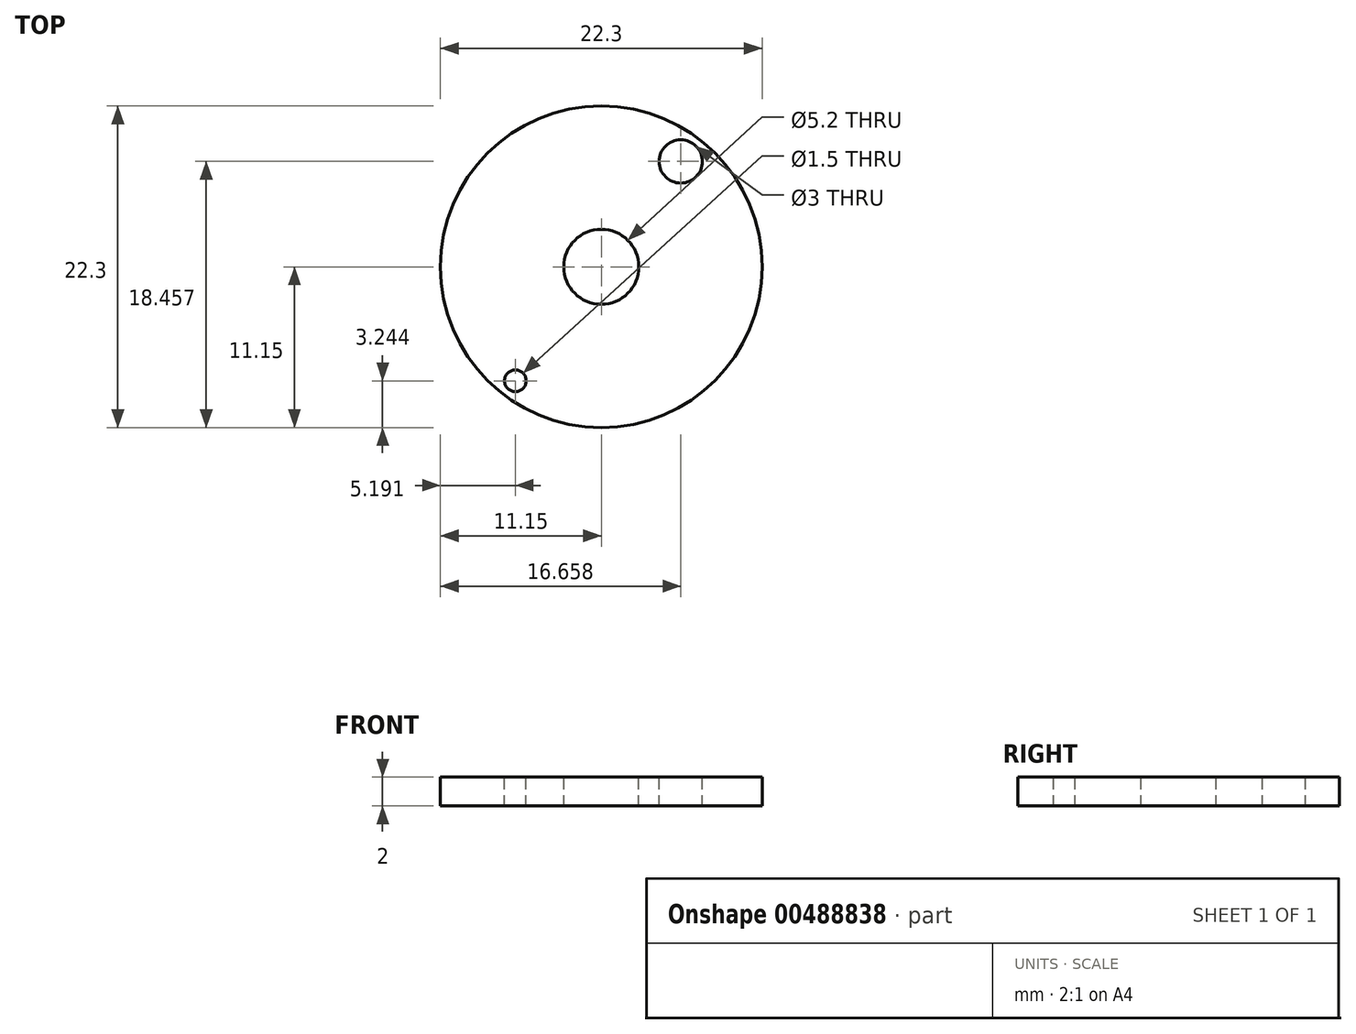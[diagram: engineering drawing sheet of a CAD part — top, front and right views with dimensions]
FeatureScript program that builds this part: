
annotation { "Feature Type Name" : "Feature", "Feature Type Description" : "" }
export const myFeature = defineFeature(function(context is Context, id is Id, definition is map)
    precondition{}
    {
        {
            var Q0;
            Q0=qCreatedBy(makeId("Top.planeOp"),FACE);
            var sketch = newSketch(context, id + "F0", { "sketchPlane" : qUnion([Q0])});
            skCircle(sketch, "E0", {"center": v(0, 0) * mm, "radius": 11.15 * mm});
            skSolve(sketch);
        }
        {
            var Q0;
            Q0=makeQuery(id+"F0.imprint","IMPRINT",FACE,{"disambiguationData":[TD([[makeQuery(id+"F0.imprint","IMPRINT",EDGE,{"derivedFrom":sQuery(id+"F0.wireOp",EDGE,"E0")}),1.0]])]});
            extrude(context, id + "F1", {"entities" : qUnion([Q0]), "offsetDistance" : 25 * mm, "depth" : 2 * mm});
        }
        {
            var Q0;
            Q0=makeQuery(id+"F1.opExtrude","CAP_FACE",FACE,{"disambiguationData":[OSD([sQuery(id+"F0.wireOp",EDGE,"E0")])],"isStart":false});
            var sketch = newSketch(context, id + "F2", { "sketchPlane" : qUnion([Q0])});
            skCircle(sketch, "E1", {"center": v(5.5, 7.3) * mm, "radius": 1.5 * mm});
            skCircle(sketch, "E2.1.0", {"center": v(-5.96, -7.9) * mm, "radius": 0.75 * mm});
            skPoint(sketch, "E2.center", {"position": v(0, 0) * mm});
            skCircle(sketch, "E3", {"center": v(0, 0) * mm, "radius": 2.6 * mm});
            skLineSegment(sketch, "E4", {"start": v(-5.96, -7.9) * mm, "end": v(0, 0) * mm, "construction": true});
            skSolve(sketch);
        }
        {
            var Q0;
            Q0=makeQuery(id+"F2.imprint","IMPRINT",FACE,{"disambiguationData":[TD([[makeQuery(id+"F2.imprint","IMPRINT",EDGE,{"derivedFrom":sQuery(id+"F2.wireOp",EDGE,"E2.7.0")}),1.0]])]});
            var Q1;
            Q1=makeQuery(id+"F2.imprint","IMPRINT",FACE,{"disambiguationData":[TD([[makeQuery(id+"F2.imprint","IMPRINT",EDGE,{"derivedFrom":sQuery(id+"F2.wireOp",EDGE,"E1")}),1.0]])]});
            var Q2;
            Q2=makeQuery(id+"F2.imprint","IMPRINT",FACE,{"disambiguationData":[TD([[makeQuery(id+"F2.imprint","IMPRINT",EDGE,{"derivedFrom":sQuery(id+"F2.wireOp",EDGE,"E2.1.0")}),1.0]])]});
            var Q3;
            Q3=makeQuery(id+"F2.imprint","IMPRINT",FACE,{"disambiguationData":[TD([[makeQuery(id+"F2.imprint","IMPRINT",EDGE,{"derivedFrom":sQuery(id+"F2.wireOp",EDGE,"E2.2.0")}),1.0]])]});
            var Q4;
            Q4=makeQuery(id+"F2.imprint","IMPRINT",FACE,{"disambiguationData":[TD([[makeQuery(id+"F2.imprint","IMPRINT",EDGE,{"derivedFrom":sQuery(id+"F2.wireOp",EDGE,"E2.3.0")}),1.0]])]});
            var Q5;
            Q5=makeQuery(id+"F2.imprint","IMPRINT",FACE,{"disambiguationData":[TD([[makeQuery(id+"F2.imprint","IMPRINT",EDGE,{"derivedFrom":sQuery(id+"F2.wireOp",EDGE,"E2.4.0")}),1.0]])]});
            var Q6;
            Q6=makeQuery(id+"F2.imprint","IMPRINT",FACE,{"disambiguationData":[TD([[makeQuery(id+"F2.imprint","IMPRINT",EDGE,{"derivedFrom":sQuery(id+"F2.wireOp",EDGE,"E2.6.0")}),1.0]])]});
            var Q7;
            Q7=makeQuery(id+"F2.imprint","IMPRINT",FACE,{"disambiguationData":[TD([[makeQuery(id+"F2.imprint","IMPRINT",EDGE,{"derivedFrom":sQuery(id+"F2.wireOp",EDGE,"7f0558c1-408a-4e5f-b6c5-c4e4467df889.1.11.0")}),1.0]])]});
            var Q8;
            Q8=makeQuery(id+"F2.imprint","IMPRINT",FACE,{"disambiguationData":[TD([[makeQuery(id+"F2.imprint","IMPRINT",EDGE,{"derivedFrom":sQuery(id+"F2.wireOp",EDGE,"7f0558c1-408a-4e5f-b6c5-c4e4467df889.1.10.0")}),1.0]])]});
            var Q9;
            Q9=makeQuery(id+"F2.imprint","IMPRINT",FACE,{"disambiguationData":[TD([[makeQuery(id+"F2.imprint","IMPRINT",EDGE,{"derivedFrom":sQuery(id+"F2.wireOp",EDGE,"7f0558c1-408a-4e5f-b6c5-c4e4467df889.1.7.0")}),1.0]])]});
            var Q10;
            Q10=makeQuery(id+"F2.imprint","IMPRINT",FACE,{"disambiguationData":[TD([[makeQuery(id+"F2.imprint","IMPRINT",EDGE,{"derivedFrom":sQuery(id+"F2.wireOp",EDGE,"E2.5.0")}),1.0]])]});
            var Q11;
            Q11=makeQuery(id+"F2.imprint","IMPRINT",FACE,{"disambiguationData":[TD([[makeQuery(id+"F2.imprint","IMPRINT",EDGE,{"derivedFrom":sQuery(id+"F2.wireOp",EDGE,"7f0558c1-408a-4e5f-b6c5-c4e4467df889.1.6.0")}),1.0]])]});
            var Q12;
            Q12=makeQuery(id+"F2.imprint","IMPRINT",FACE,{"disambiguationData":[TD([[makeQuery(id+"F2.imprint","IMPRINT",EDGE,{"derivedFrom":sQuery(id+"F2.wireOp",EDGE,"7f0558c1-408a-4e5f-b6c5-c4e4467df889.1.9.0")}),1.0]])]});
            var Q13;
            Q13=makeQuery(id+"F2.imprint","IMPRINT",FACE,{"disambiguationData":[TD([[makeQuery(id+"F2.imprint","IMPRINT",EDGE,{"derivedFrom":sQuery(id+"F2.wireOp",EDGE,"7f0558c1-408a-4e5f-b6c5-c4e4467df889.1.8.0")}),1.0]])]});
            var Q14;
            Q14=makeQuery(id+"F2.imprint","IMPRINT",FACE,{"disambiguationData":[TD([[makeQuery(id+"F2.imprint","IMPRINT",EDGE,{"derivedFrom":sQuery(id+"F2.wireOp",EDGE,"E3")}),1.0]])]});
            extrude(context, id + "F3", {"entities" : qUnion([Q0, Q1, Q2, Q3, Q4, Q5, Q6, Q7, Q8, Q9, Q10, Q11, Q12, Q13, Q14]), "operationType" : NewBodyOperationType.REMOVE, "oppositeDirection" : true, "depth" : 25 * mm});
        }
    });
